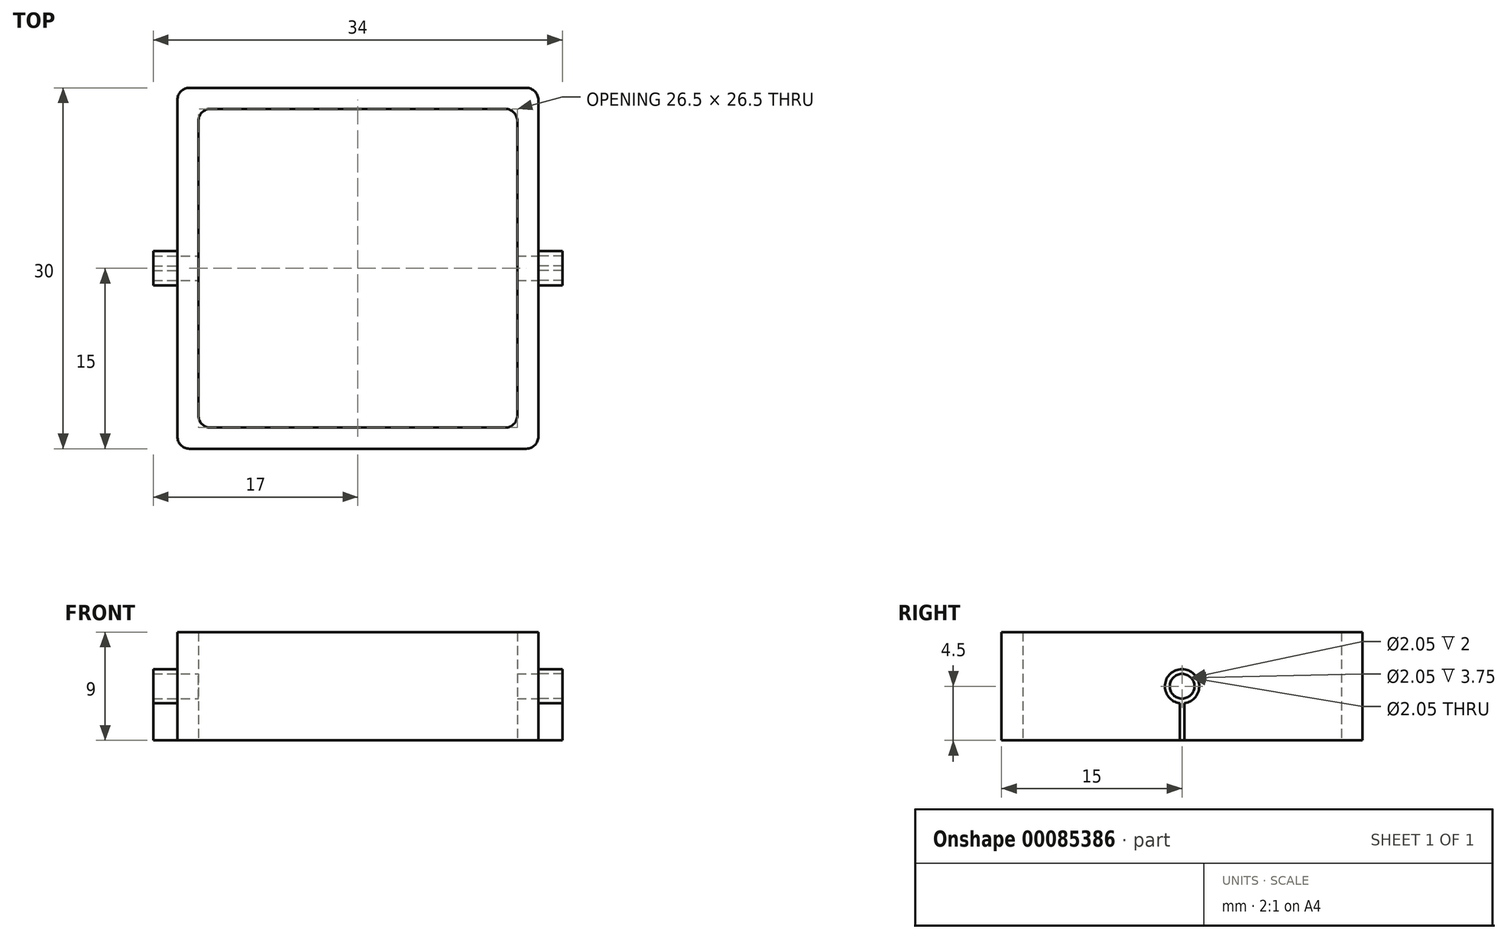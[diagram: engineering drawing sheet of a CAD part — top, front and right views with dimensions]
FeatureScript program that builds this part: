
annotation { "Feature Type Name" : "Feature", "Feature Type Description" : "" }
export const myFeature = defineFeature(function(context is Context, id is Id, definition is map)
    precondition{}
    {
        {
            var Q0;
            Q0=qCreatedBy(makeId("Top.planeOp"),FACE);
            var sketch = newSketch(context, id + "F0", { "sketchPlane" : qUnion([Q0])});
            skLineSegment(sketch, "E0", {"start": v(0, 0) * mm, "end": v(13.25, 0) * mm});
            skLineSegment(sketch, "E1", {"start": v(13.25, 0) * mm, "end": v(13.25, 13.25) * mm});
            skLineSegment(sketch, "E2.bottom", {"start": v(12.25, 13.25) * mm, "end": v(-12.25, 13.25) * mm});
            skLineSegment(sketch, "E2.top", {"start": v(12.25, -13.25) * mm, "end": v(-12.25, -13.25) * mm});
            skLineSegment(sketch, "E2.left", {"start": v(13.25, 12.25) * mm, "end": v(13.25, -12.25) * mm});
            skLineSegment(sketch, "E2.right", {"start": v(-13.25, 12.25) * mm, "end": v(-13.25, -12.25) * mm});
            skLineSegment(sketch, "E3", {"start": v(13.25, 0) * mm, "end": v(15, 0) * mm});
            skLineSegment(sketch, "E4", {"start": v(15, 0) * mm, "end": v(15, 15) * mm});
            skLineSegment(sketch, "E5.bottom", {"start": v(14, 15) * mm, "end": v(-14, 15) * mm});
            skLineSegment(sketch, "E5.top", {"start": v(14, -15) * mm, "end": v(-14, -15) * mm});
            skLineSegment(sketch, "E5.left", {"start": v(15, 14) * mm, "end": v(15, -14) * mm});
            skLineSegment(sketch, "E5.right", {"start": v(-15, 14) * mm, "end": v(-15, -14) * mm});
            skPoint(sketch, "E6.visualSharp", {"position": v(13.25, 13.25) * mm});
            skArc(sketch, "E6.filletArc", {"start": v(13.25, 12.25) * mm, "mid": v(12.96, 12.96) * mm, "end": v(12.25, 13.25) * mm});
            skPoint(sketch, "E7.visualSharp", {"position": v(13.25, -13.25) * mm});
            skArc(sketch, "E7.filletArc", {"start": v(12.25, -13.25) * mm, "mid": v(12.96, -12.96) * mm, "end": v(13.25, -12.25) * mm});
            skPoint(sketch, "E8.visualSharp", {"position": v(-13.25, -13.25) * mm});
            skArc(sketch, "E8.filletArc", {"start": v(-13.25, -12.25) * mm, "mid": v(-12.96, -12.96) * mm, "end": v(-12.25, -13.25) * mm});
            skPoint(sketch, "E9.visualSharp", {"position": v(-13.25, 13.25) * mm});
            skArc(sketch, "E9.filletArc", {"start": v(-12.25, 13.25) * mm, "mid": v(-12.96, 12.96) * mm, "end": v(-13.25, 12.25) * mm});
            skPoint(sketch, "E10.visualSharp", {"position": v(15, 15) * mm});
            skArc(sketch, "E10.filletArc", {"start": v(15, 14) * mm, "mid": v(14.7, 14.7) * mm, "end": v(14, 15) * mm});
            skPoint(sketch, "E11.visualSharp", {"position": v(15, -15) * mm});
            skArc(sketch, "E11.filletArc", {"start": v(14, -15) * mm, "mid": v(14.7, -14.7) * mm, "end": v(15, -14) * mm});
            skPoint(sketch, "E12.visualSharp", {"position": v(-15, -15) * mm});
            skArc(sketch, "E12.filletArc", {"start": v(-15, -14) * mm, "mid": v(-14.7, -14.7) * mm, "end": v(-14, -15) * mm});
            skPoint(sketch, "E13.visualSharp", {"position": v(-15, 15) * mm});
            skArc(sketch, "E13.filletArc", {"start": v(-14, 15) * mm, "mid": v(-14.7, 14.7) * mm, "end": v(-15, 14) * mm});
            skSolve(sketch);
        }
        {
            var Q0;
            Q0 = qSketchRegion(id + "F0", true);
            extrude(context, id + "F1", {"entities" : qUnion([Q0]), "depth" : 9 * mm});
        }
        {
            var Q0;
            Q0=makeQuery(id+"F1.opExtrude","SWEPT_FACE",FACE,{"disambiguationData":[OSD([sQuery(id+"F0.wireOp",EDGE,"E5.left")])]});
            var sketch = newSketch(context, id + "F2", { "sketchPlane" : qUnion([Q0])});
            skLineSegment(sketch, "E14", {"start": v(0, 0) * mm, "end": v(0, 4.5) * mm});
            skCircle(sketch, "E15", {"center": v(0, 4.5) * mm, "radius": 1.43 * mm});
            skCircle(sketch, "E16", {"center": v(0, 4.5) * mm, "radius": 1.02 * mm});
            skLineSegment(sketch, "E17.top", {"start": v(0.2, 0) * mm, "end": v(-0.2, 0) * mm});
            skLineSegment(sketch, "E17.left", {"start": v(0.2, 3.09) * mm, "end": v(0.2, 0) * mm});
            skLineSegment(sketch, "E17.right", {"start": v(-0.2, 3.09) * mm, "end": v(-0.2, 0) * mm});
            skSolve(sketch);
        }
        {
            var Q0;
            Q0=makeQuery(id+"F2.imprint","IMPRINT",FACE,{"disambiguationData":[TD([[makeQuery(id+"F2.imprint","IMPRINT",EDGE,{"derivedFrom":sQuery(id+"F2.wireOp",EDGE,"E16")}),1.0]])]});
            extrude(context, id + "F3", {"entities" : qUnion([Q0]), "operationType" : NewBodyOperationType.REMOVE, "endBound" : BoundingType.THROUGH_ALL, "oppositeDirection" : true, "depth" : 25 * mm});
        }
        {
            var Q0;
            Q0=makeQuery(id+"F2.imprint","IMPRINT",FACE,{"disambiguationData":[TD([[makeQuery(id+"F2.imprint","IMPRINT",EDGE,{"derivedFrom":sQuery(id+"F2.wireOp",EDGE,"E15")}),1.0]])]});
            var Q1;
            {var subQ5=sQuery(id+"F2.wireOp",EDGE,"E17.right");Q1=makeQuery(id+"F2.imprint","IMPRINT",FACE,{"disambiguationData":[TD([[makeQuery(id+"F2.imprint","IMPRINT",EDGE,{"derivedFrom":subQ5}),1.0]])]});}
            var Q2;
            {var subQ5=sQuery(id+"F2.wireOp",EDGE,"E17.left");Q2=makeQuery(id+"F2.imprint","IMPRINT",FACE,{"disambiguationData":[TD([[makeQuery(id+"F2.imprint","IMPRINT",EDGE,{"derivedFrom":subQ5}),-1.0]])]});}
            var Q3;
            Q3=sQuery(id+"F2.wireOp",EDGE,"E15");
            extrude(context, id + "F4", {"entities" : qUnion([Q0, Q1, Q2]), "surfaceEntities" : qUnion([Q3]), "depth" : 2 * mm});
        }
        {
            var Q0;
            Q0=makeQuery(id+"F1.opExtrude","SWEPT_FACE",FACE,{"disambiguationData":[OSD([sQuery(id+"F0.wireOp",EDGE,"E5.right")])]});
            var sketch = newSketch(context, id + "F5", { "sketchPlane" : qUnion([Q0])});
            skCircle(sketch, "E18", {"center": v(0, 4.5) * mm, "radius": 1.43 * mm});
            skCircle(sketch, "E19", {"center": v(0, 4.5) * mm, "radius": 1.02 * mm});
            skLineSegment(sketch, "E20.bottom", {"start": v(0.2, 3.09) * mm, "end": v(-0.2, 3.09) * mm});
            skLineSegment(sketch, "E20.top", {"start": v(0.2, 0) * mm, "end": v(-0.2, 0) * mm});
            skLineSegment(sketch, "E20.left", {"start": v(0.2, 3.09) * mm, "end": v(0.2, 0) * mm});
            skLineSegment(sketch, "E20.right", {"start": v(-0.2, 3.09) * mm, "end": v(-0.2, 0) * mm});
            skSolve(sketch);
        }
        {
            var Q0;
            Q0 = qSketchRegion(id + "F5", true);
            extrude(context, id + "F6", {"entities" : qUnion([Q0]), "operationType" : NewBodyOperationType.ADD, "depth" : 2 * mm});
        }
    });
